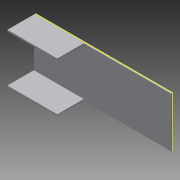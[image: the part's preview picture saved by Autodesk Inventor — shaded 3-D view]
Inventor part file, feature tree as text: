
AUTODESK INVENTOR PART (.ipt)
format: ipt  version: 2013 (Build 170138000, 138)  size: 97,280 bytes
history: native  units: in
note: dims shown in document units (in); Inventor stores cm internally (conversion verified against a paired STEP export)
features: other x4, reference x4, sketch x2, extrude x1
ambient origin geometry x8: Origin, YZ Plane, XZ Plane, XY Plane, X Axis, Y Axis, Z Axis, Center Point
bodies: Solid1 (feature_tree)
feature tree (11):
  other  "Table"
  other  "channel2.25x4.ipt"
  extrude  "Extrusion1"  TaperAngle=0.0deg  [1 undecoded]
  sketch  "Sketch2"  dims[d5=1.0in d6=0.0in d7=4.0in]
  other  "Solid1::channel2.25x4.ipt"
  other  "TaggingFeature1"
  sketch  "Sketch1"  dims[d0=4.0in d1=2.25in d2=0.125in d4=0.0in]
  reference  "Reference1"
  reference  "Reference2"
  reference  "Reference3"
  reference  "Reference4"
note: 1 required parameter value undecoded (feature->parameter linkage not recoverable at this tier; creation-order binding heuristic only, values carry confidence <= 0.55)
